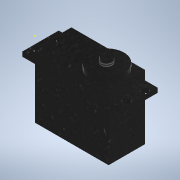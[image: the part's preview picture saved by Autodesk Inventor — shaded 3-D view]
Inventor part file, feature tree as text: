
AUTODESK INVENTOR PART (.ipt)
format: ipt  version: 2021 (Build 250183000, 183)  size: 171,008 bytes
history: native  units: mm
features: sketch x7, extrude x6, other x1, hole x1, thread x1
ambient origin geometry x8: Origin, YZ Plane, XZ Plane, XY Plane, X Axis, Y Axis, Z Axis, Center Point
bodies: Body1 (feature_tree)
feature tree (16):
  other  "Sólido1"
  extrude  "Extrusión1"  Depth=20.0mm TaperAngle=0.0deg
  extrude  "Extrusión2"  Depth=3.0mm TaperAngle=0.0deg
  extrude  "Extrusión3"  Depth=3.0mm TaperAngle=0.0deg
  hole  "Agujero1"  [1 undecoded]
  sketch  "Boceto5"  dims[d44=2.0mm d45=0.0mm d18=1.0mm]
  extrude  "Extrusión4"  Depth=1.0mm
  extrude  "Extrusión5"  Depth=0.375mm
  extrude  "Extrusión6"  Depth=0.5mm
  thread  "Rosca1"  [1 undecoded]
  sketch  "Boceto7"  dims[d21=0.15mm d29=0.375mm d31=0.5mm d32=0.872665mm d33=0.5mm d34=0.872665mm]
  sketch  "Boceto1"  dims[d2=20.0mm d3=0.0mm d7=20.0mm d8=0.0mm]
  sketch  "Boceto2"  dims[d11=20.0mm d12=0.0mm]
  sketch  "Boceto3"  dims[d22=4.0mm d23=6.0mm d24=4.0mm d25=2.0mm d26=90.0deg d27=8.0mm d28=20.594885mm d37=3.0mm d38=0.0mm]
  sketch  "Boceto4"  dims[d39=2.0mm d40=0.0mm d42=3.0mm d43=0.0mm]
  sketch  "Boceto6"  dims[d19=1.0mm d20=1.0mm]
note: 2 required parameter values undecoded (feature->parameter linkage not recoverable at this tier; creation-order binding heuristic only, values carry confidence <= 0.55)
